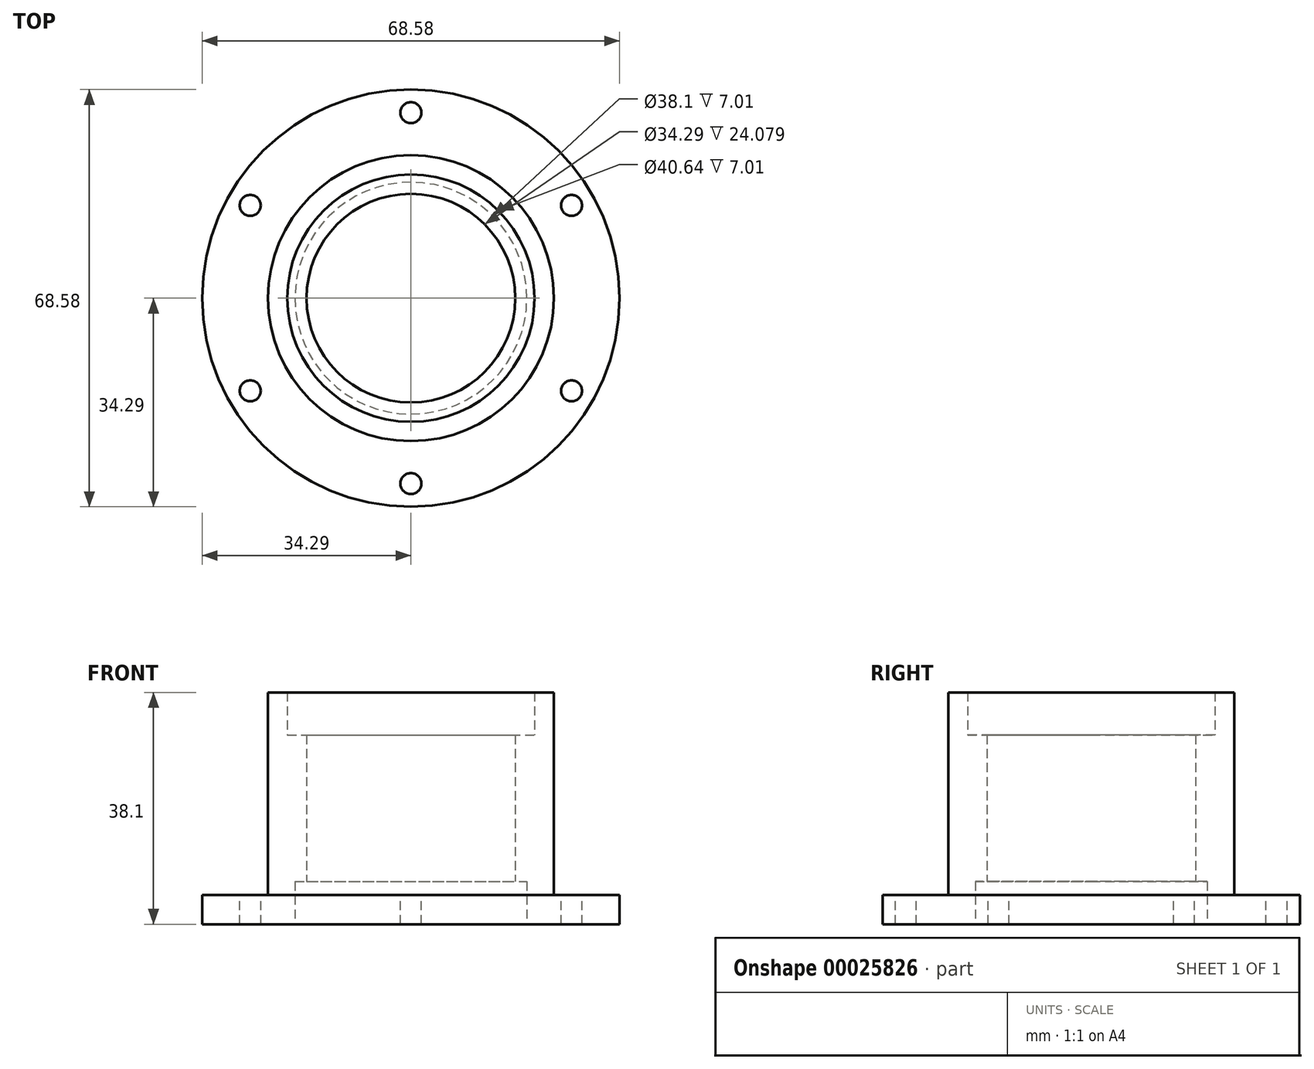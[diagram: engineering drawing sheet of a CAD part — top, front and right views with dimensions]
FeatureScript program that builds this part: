
annotation { "Feature Type Name" : "Feature", "Feature Type Description" : "" }
export const myFeature = defineFeature(function(context is Context, id is Id, definition is map)
    precondition{}
    {
        {
            var Q0;
            Q0=qCreatedBy(makeId("Front.planeOp"),FACE);
            var sketch = newSketch(context, id + "F0", { "sketchPlane" : qUnion([Q0])});
            skLineSegment(sketch, "E0", {"start": v(0, 0) * mm, "end": v(0, 42.85) * mm, "construction": true});
            skLineSegment(sketch, "E1", {"start": v(0, 0) * mm, "end": v(-19.05, 0) * mm, "construction": true});
            skLineSegment(sketch, "E2", {"start": v(-34.3, 4.78) * mm, "end": v(-23.5, 4.78) * mm});
            skLineSegment(sketch, "E3", {"start": v(-23.5, 4.78) * mm, "end": v(-23.5, 38.1) * mm});
            skLineSegment(sketch, "E4", {"start": v(-23.5, 38.1) * mm, "end": v(-20.32, 38.1) * mm});
            skLineSegment(sketch, "E5", {"start": v(-20.32, 38.1) * mm, "end": v(-20.32, 31.09) * mm});
            skLineSegment(sketch, "E6", {"start": v(-20.32, 31.09) * mm, "end": v(-17.15, 31.09) * mm});
            skLineSegment(sketch, "E7", {"start": v(-17.15, 31.09) * mm, "end": v(-17.15, 7.01) * mm});
            skLineSegment(sketch, "E8", {"start": v(-17.15, 7.01) * mm, "end": v(-19.05, 7.01) * mm});
            skLineSegment(sketch, "E9", {"start": v(-19.05, 7.01) * mm, "end": v(-19.05, 0) * mm});
            skLineSegment(sketch, "E10", {"start": v(-19.05, 0) * mm, "end": v(-34.3, 0) * mm});
            skLineSegment(sketch, "E11", {"start": v(-34.3, 0) * mm, "end": v(-34.3, 4.78) * mm});
            skSolve(sketch);
        }
        {
            var Q0;
            Q0=makeQuery(id+"F0.imprint","IMPRINT",FACE,{"disambiguationData":[TD([[makeQuery(id+"F0.imprint","IMPRINT",EDGE,{"derivedFrom":sQuery(id+"F0.wireOp",EDGE,"E2")}),-1.0]])]});
            var Q1;
            Q1=sQuery(id+"F0.wireOp",EDGE,"E0");
            revolve(context, id + "F1", {"entities" : qUnion([Q0]), "axis" : qUnion([Q1]), "revolveType" : RevolveType.FULL});
        }
        {
            var Q0;
            Q0=makeQuery(id+"F1.opRevolve","SWEPT_FACE",FACE,{"disambiguationData":[OSD([sQuery(id+"F0.wireOp",EDGE,"E2")])]});
            var sketch = newSketch(context, id + "F2", { "sketchPlane" : qUnion([Q0])});
            skLineSegment(sketch, "E12", {"start": v(0, 0) * mm, "end": v(0, 30.48) * mm});
            skLineSegment(sketch, "E13.1.0", {"start": v(0, 0) * mm, "end": v(-26.4, 15.24) * mm});
            skLineSegment(sketch, "E13.2.0", {"start": v(0, 0) * mm, "end": v(-26.4, -15.24) * mm});
            skLineSegment(sketch, "E13.3.0", {"start": v(0, 0) * mm, "end": v(0, -30.48) * mm});
            skLineSegment(sketch, "E13.4.0", {"start": v(0, 0) * mm, "end": v(26.4, -15.24) * mm});
            skLineSegment(sketch, "E13.5.0", {"start": v(0, 0) * mm, "end": v(26.4, 15.24) * mm});
            skPoint(sketch, "E13.center", {"position": v(0, 0) * mm});
            skSolve(sketch);
        }
        {
            var Q0;
            Q0=sQuery(id+"F2.wireOp",VERTEX,"E13.1.0.end");
            var Q1;
            Q1=sQuery(id+"F2.wireOp",VERTEX,"E12.end");
            var Q2;
            Q2=sQuery(id+"F2.wireOp",VERTEX,"E13.5.0.end");
            var Q3;
            Q3=sQuery(id+"F2.wireOp",VERTEX,"E13.4.0.end");
            var Q4;
            Q4=sQuery(id+"F2.wireOp",VERTEX,"E13.3.0.end");
            var Q5;
            Q5=sQuery(id+"F2.wireOp",VERTEX,"E13.2.0.end");
            var Q6;
            Q6=makeQuery(id+"F1.opRevolve","SWEPT_BODY",BODY,{"disambiguationData":[OSD([sQuery(id+"F0.wireOp",EDGE,"E2"),sQuery(id+"F0.wireOp",EDGE,"E3"),sQuery(id+"F0.wireOp",EDGE,"E4"),sQuery(id+"F0.wireOp",EDGE,"E5"),sQuery(id+"F0.wireOp",EDGE,"E6"),sQuery(id+"F0.wireOp",EDGE,"E7"),sQuery(id+"F0.wireOp",EDGE,"E8"),sQuery(id+"F0.wireOp",EDGE,"E9"),sQuery(id+"F0.wireOp",EDGE,"E10"),sQuery(id+"F0.wireOp",EDGE,"E11")])]});
            hole(context, id + "F3", {"style" : HoleStyle.SIMPLE, "holeDiameter" : 3.45 * mm, "endStyle" : HoleEndStyle.THROUGH, "locations" : qUnion([Q0, Q1, Q2, Q3, Q4, Q5]), "scope" : qUnion([Q6])});
        }
    });
